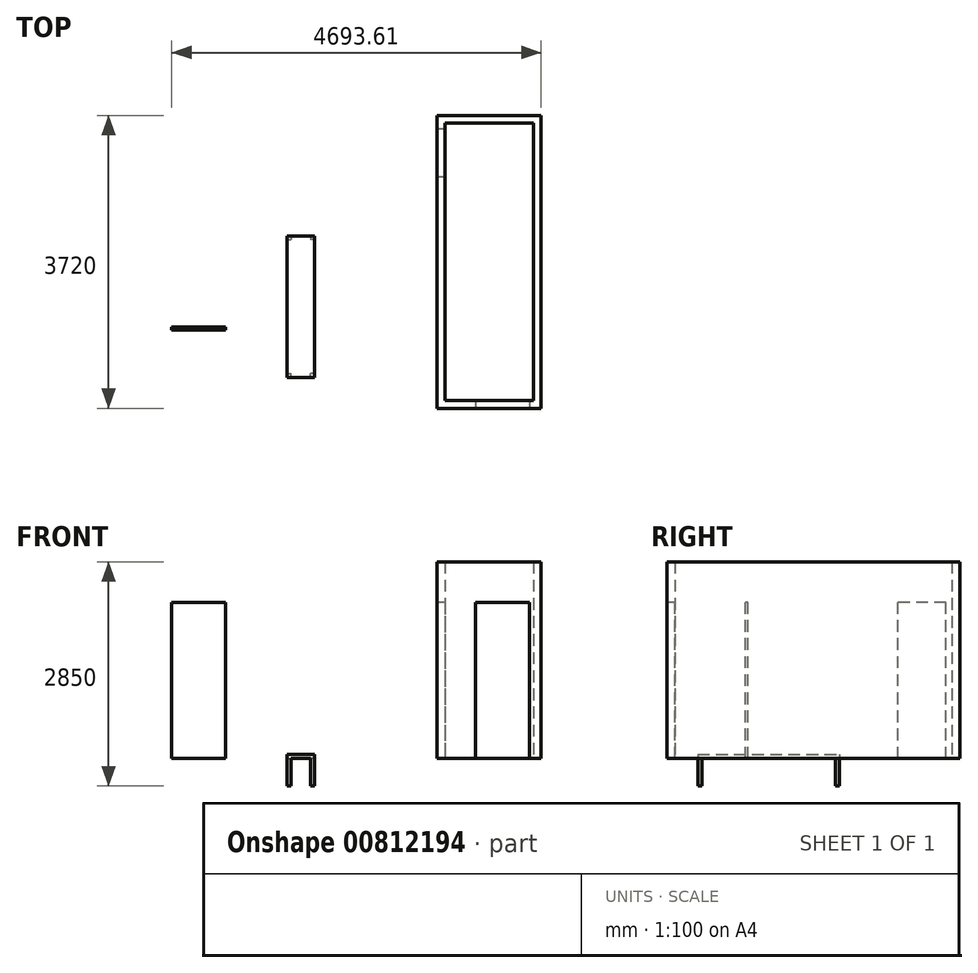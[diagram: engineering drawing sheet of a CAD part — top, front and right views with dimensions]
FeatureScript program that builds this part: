
annotation { "Feature Type Name" : "Feature", "Feature Type Description" : "" }
export const myFeature = defineFeature(function(context is Context, id is Id, definition is map)
    precondition{}
    {
        {
            var Q0;
            Q0=qCreatedBy(makeId("Top.planeOp"),FACE);
            var sketch = newSketch(context, id + "F0", { "sketchPlane" : qUnion([Q0])});
            skLineSegment(sketch, "E0.bottom", {"start": v(521.72, -893.83) * mm, "end": v(1641.72, -893.83) * mm});
            skLineSegment(sketch, "E0.top", {"start": v(521.72, 2626.17) * mm, "end": v(1641.72, 2626.17) * mm});
            skLineSegment(sketch, "E0.left", {"start": v(521.72, -893.83) * mm, "end": v(521.72, 2626.17) * mm});
            skLineSegment(sketch, "E0.right", {"start": v(1641.72, -893.83) * mm, "end": v(1641.72, 2626.17) * mm});
            skLineSegment(sketch, "E1.0", {"start": v(421.72, -993.83) * mm, "end": v(421.72, 2726.17) * mm});
            skLineSegment(sketch, "E1.1", {"start": v(421.72, -993.83) * mm, "end": v(1741.72, -993.83) * mm});
            skLineSegment(sketch, "E1.2", {"start": v(1741.72, -993.83) * mm, "end": v(1741.72, 2726.17) * mm});
            skLineSegment(sketch, "E1.3", {"start": v(421.72, 2726.17) * mm, "end": v(1741.72, 2726.17) * mm});
            skSolve(sketch);
        }
        {
            var Q0;
            Q0=makeQuery(id+"F0.imprint","IMPRINT",FACE,{"disambiguationData":[TD([[makeQuery(id+"F0.imprint","IMPRINT",EDGE,{"derivedFrom":sQuery(id+"F0.wireOp",EDGE,"E0.bottom")}),-1.0]])]});
            extrude(context, id + "F1", {"entities" : qUnion([Q0]), "depth" : 2500 * mm, "offsetDistance" : 25 * mm});
        }
        {
            var Q0;
            Q0=makeQuery(id+"F1.opExtrude","SWEPT_FACE",FACE,{"disambiguationData":[OSD([sQuery(id+"F0.wireOp",EDGE,"E1.1")])]});
            var sketch = newSketch(context, id + "F2", { "sketchPlane" : qUnion([Q0])});
            skLineSegment(sketch, "E2.bottom", {"start": v(910.72, 0) * mm, "end": v(1591.72, 0) * mm});
            skLineSegment(sketch, "E2.top", {"start": v(910.72, 1981) * mm, "end": v(1591.72, 1981) * mm});
            skLineSegment(sketch, "E2.left", {"start": v(910.72, 0) * mm, "end": v(910.72, 1981) * mm});
            skLineSegment(sketch, "E2.right", {"start": v(1591.72, 0) * mm, "end": v(1591.72, 1981) * mm});
            skSolve(sketch);
        }
        {
            var Q0;
            Q0=makeQuery(id+"F2.imprint","IMPRINT",FACE,{"disambiguationData":[TD([[makeQuery(id+"F2.imprint","IMPRINT",EDGE,{"derivedFrom":sQuery(id+"F2.wireOp",EDGE,"E2.bottom")}),1.0]])]});
            extrude(context, id + "F3", {"entities" : qUnion([Q0]), "operationType" : NewBodyOperationType.REMOVE, "endBound" : BoundingType.UP_TO_NEXT, "oppositeDirection" : true, "depth" : 25 * mm, "offsetDistance" : 25 * mm});
        }
        {
            var Q0;
            Q0=qCreatedBy(makeId("Top.planeOp"),FACE);
            var sketch = newSketch(context, id + "F4", { "sketchPlane" : qUnion([Q0])});
            skLineSegment(sketch, "E3.bottom", {"start": v(-1487.08, -603.87) * mm, "end": v(-1137.08, -603.87) * mm});
            skLineSegment(sketch, "E3.top", {"start": v(-1487.08, 1196.13) * mm, "end": v(-1137.08, 1196.13) * mm});
            skLineSegment(sketch, "E3.left", {"start": v(-1487.08, -603.87) * mm, "end": v(-1487.08, 1196.13) * mm});
            skLineSegment(sketch, "E3.right", {"start": v(-1137.08, -603.87) * mm, "end": v(-1137.08, 1196.13) * mm});
            skSolve(sketch);
        }
        {
            var Q0;
            Q0=makeQuery(id+"F4.imprint","IMPRINT",FACE,{"disambiguationData":[TD([[makeQuery(id+"F4.imprint","IMPRINT",EDGE,{"derivedFrom":sQuery(id+"F4.wireOp",EDGE,"E3.bottom")}),1.0]])]});
            extrude(context, id + "F5", {"entities" : qUnion([Q0]), "depth" : 50 * mm, "offsetDistance" : 25 * mm});
        }
        {
            var Q0;
            Q0=makeQuery(id+"F5.opExtrude","CAP_FACE",FACE,{"disambiguationData":[OSD([sQuery(id+"F4.wireOp",EDGE,"E3.bottom"),sQuery(id+"F4.wireOp",EDGE,"E3.top"),sQuery(id+"F4.wireOp",EDGE,"E3.left"),sQuery(id+"F4.wireOp",EDGE,"E3.right")])],"isStart":true});
            var sketch = newSketch(context, id + "F6", { "sketchPlane" : qUnion([Q0])});
            skLineSegment(sketch, "E4.bottom", {"start": v(-1487.08, 603.87) * mm, "end": v(-1437.08, 603.87) * mm});
            skLineSegment(sketch, "E4.top", {"start": v(-1487.08, 553.87) * mm, "end": v(-1437.08, 553.87) * mm});
            skLineSegment(sketch, "E4.left", {"start": v(-1487.08, 603.87) * mm, "end": v(-1487.08, 553.87) * mm});
            skLineSegment(sketch, "E4.right", {"start": v(-1437.08, 603.87) * mm, "end": v(-1437.08, 553.87) * mm});
            skLineSegment(sketch, "E5.bottom", {"start": v(-1137.08, 603.87) * mm, "end": v(-1187.08, 603.87) * mm});
            skLineSegment(sketch, "E5.top", {"start": v(-1137.08, 553.87) * mm, "end": v(-1187.08, 553.87) * mm});
            skLineSegment(sketch, "E5.left", {"start": v(-1137.08, 603.87) * mm, "end": v(-1137.08, 553.87) * mm});
            skLineSegment(sketch, "E5.right", {"start": v(-1187.08, 603.87) * mm, "end": v(-1187.08, 553.87) * mm});
            skLineSegment(sketch, "E6.bottom", {"start": v(-1487.08, -1196.13) * mm, "end": v(-1437.08, -1196.13) * mm});
            skLineSegment(sketch, "E6.top", {"start": v(-1487.08, -1146.13) * mm, "end": v(-1437.08, -1146.13) * mm});
            skLineSegment(sketch, "E6.left", {"start": v(-1487.08, -1196.13) * mm, "end": v(-1487.08, -1146.13) * mm});
            skLineSegment(sketch, "E6.right", {"start": v(-1437.08, -1196.13) * mm, "end": v(-1437.08, -1146.13) * mm});
            skLineSegment(sketch, "E7.bottom", {"start": v(-1137.08, -1196.13) * mm, "end": v(-1187.08, -1196.13) * mm});
            skLineSegment(sketch, "E7.top", {"start": v(-1137.08, -1146.13) * mm, "end": v(-1187.08, -1146.13) * mm});
            skLineSegment(sketch, "E7.left", {"start": v(-1137.08, -1196.13) * mm, "end": v(-1137.08, -1146.13) * mm});
            skLineSegment(sketch, "E7.right", {"start": v(-1187.08, -1196.13) * mm, "end": v(-1187.08, -1146.13) * mm});
            skSolve(sketch);
        }
        {
            var Q0;
            Q0=makeQuery(id+"F6.imprint","IMPRINT",FACE,{"disambiguationData":[TD([[makeQuery(id+"F6.imprint","IMPRINT",EDGE,{"derivedFrom":sQuery(id+"F6.wireOp",EDGE,"E4.bottom")}),-1.0]])]});
            var Q1;
            Q1=makeQuery(id+"F6.imprint","IMPRINT",FACE,{"disambiguationData":[TD([[makeQuery(id+"F6.imprint","IMPRINT",EDGE,{"derivedFrom":sQuery(id+"F6.wireOp",EDGE,"E5.bottom")}),-1.0]])]});
            var Q2;
            Q2=makeQuery(id+"F6.imprint","IMPRINT",FACE,{"disambiguationData":[TD([[makeQuery(id+"F6.imprint","IMPRINT",EDGE,{"derivedFrom":sQuery(id+"F6.wireOp",EDGE,"E7.bottom")}),1.0]])]});
            var Q3;
            Q3=makeQuery(id+"F6.imprint","IMPRINT",FACE,{"disambiguationData":[TD([[makeQuery(id+"F6.imprint","IMPRINT",EDGE,{"derivedFrom":sQuery(id+"F6.wireOp",EDGE,"E6.bottom")}),1.0]])]});
            extrude(context, id + "F7", {"entities" : qUnion([Q0, Q1, Q2, Q3]), "operationType" : NewBodyOperationType.ADD, "depth" : 350 * mm, "offsetDistance" : 25 * mm});
        }
        {
            var Q0;
            Q0=makeQuery(id+"F1.opExtrude","SWEPT_FACE",FACE,{"disambiguationData":[OSD([sQuery(id+"F0.wireOp",EDGE,"E1.0")])]});
            var sketch = newSketch(context, id + "F8", { "sketchPlane" : qUnion([Q0])});
            skLineSegment(sketch, "E8.bottom", {"start": v(-2550.17, 0) * mm, "end": v(-1940.17, 0) * mm});
            skLineSegment(sketch, "E8.top", {"start": v(-2550.17, 1981) * mm, "end": v(-1940.17, 1981) * mm});
            skLineSegment(sketch, "E8.left", {"start": v(-2550.17, 0) * mm, "end": v(-2550.17, 1981) * mm});
            skLineSegment(sketch, "E8.right", {"start": v(-1940.17, 0) * mm, "end": v(-1940.17, 1981) * mm});
            skSolve(sketch);
        }
        {
            var Q0;
            Q0=makeQuery(id+"F8.imprint","IMPRINT",FACE,{"disambiguationData":[TD([[makeQuery(id+"F8.imprint","IMPRINT",EDGE,{"derivedFrom":sQuery(id+"F8.wireOp",EDGE,"E8.bottom")}),-1.0]])]});
            extrude(context, id + "F9", {"entities" : qUnion([Q0]), "operationType" : NewBodyOperationType.REMOVE, "endBound" : BoundingType.UP_TO_NEXT, "oppositeDirection" : true, "depth" : 60 * mm, "offsetDistance" : 25 * mm});
        }
        {
            var Q0;
            Q0=qCreatedBy(makeId("Front.planeOp"),FACE);
            var sketch = newSketch(context, id + "F10", { "sketchPlane" : qUnion([Q0])});
            skLineSegment(sketch, "E9.bottom", {"start": v(-2951.89, 0) * mm, "end": v(-2265.89, 0) * mm});
            skLineSegment(sketch, "E9.top", {"start": v(-2951.89, 1981) * mm, "end": v(-2265.89, 1981) * mm});
            skLineSegment(sketch, "E9.left", {"start": v(-2951.89, 0) * mm, "end": v(-2951.89, 1981) * mm});
            skLineSegment(sketch, "E9.right", {"start": v(-2265.89, 0) * mm, "end": v(-2265.89, 1981) * mm});
            skSolve(sketch);
        }
        {
            var Q0;
            Q0=makeQuery(id+"F10.imprint","IMPRINT",FACE,{"disambiguationData":[TD([[makeQuery(id+"F10.imprint","IMPRINT",EDGE,{"derivedFrom":sQuery(id+"F10.wireOp",EDGE,"E9.bottom")}),1.0]])]});
            extrude(context, id + "F11", {"entities" : qUnion([Q0]), "oppositeDirection" : true, "depth" : 35 * mm, "offsetDistance" : 25 * mm});
        }
    });
